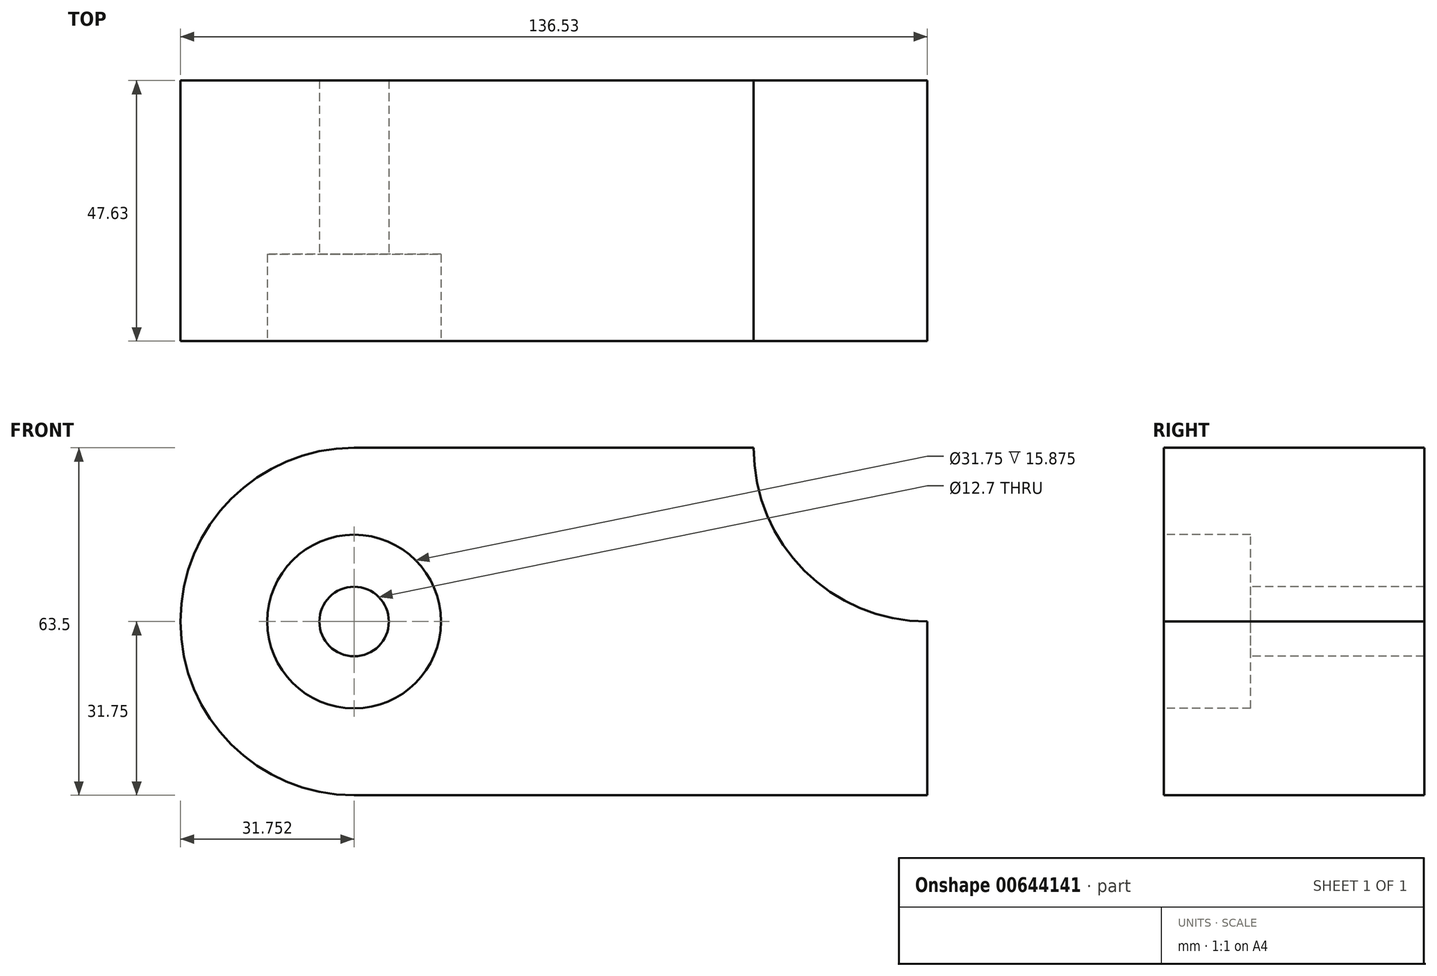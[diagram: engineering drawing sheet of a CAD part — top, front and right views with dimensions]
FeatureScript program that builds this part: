
annotation { "Feature Type Name" : "Feature", "Feature Type Description" : "" }
export const myFeature = defineFeature(function(context is Context, id is Id, definition is map)
    precondition{}
    {
        {
            var Q0;
            Q0=qCreatedBy(makeId("Front.planeOp"),FACE);
            var sketch = newSketch(context, id + "F0", { "sketchPlane" : qUnion([Q0])});
            skLineSegment(sketch, "E0.bottom", {"start": v(-52.39, -31.75) * mm, "end": v(52.39, -31.75) * mm});
            skPoint(sketch, "E0.middle", {"position": v(0, 0) * mm});
            skArc(sketch, "E1", {"start": v(-52.39, -31.75) * mm, "mid": v(-84.14, 0) * mm, "end": v(-52.39, 31.75) * mm});
            skArc(sketch, "E2", {"start": v(52.39, 0) * mm, "mid": v(29.94, 9.3) * mm, "end": v(20.64, 31.75) * mm});
            skLineSegment(sketch, "E3", {"start": v(20.64, 31.75) * mm, "end": v(-52.39, 31.75) * mm});
            skLineSegment(sketch, "E4", {"start": v(52.39, 0) * mm, "end": v(52.39, -31.75) * mm});
            skSolve(sketch);
        }
        {
            var Q0;
            Q0=makeQuery(id+"F0.imprint","IMPRINT",FACE,{"disambiguationData":[TD([[makeQuery(id+"F0.imprint","IMPRINT",EDGE,{"derivedFrom":sQuery(id+"F0.wireOp",EDGE,"E0.bottom")}),1.0]])]});
            extrude(context, id + "F1", {"entities" : qUnion([Q0]), "depth" : 47.62 * mm, "offsetDistance" : 25.4 * mm});
        }
        {
            var Q0;
            Q0=makeQuery(id+"F1.opExtrude","CAP_FACE",FACE,{"disambiguationData":[OSD([sQuery(id+"F0.wireOp",EDGE,"E0.bottom"),sQuery(id+"F0.wireOp",EDGE,"E1"),sQuery(id+"F0.wireOp",EDGE,"E2"),sQuery(id+"F0.wireOp",EDGE,"E3"),sQuery(id+"F0.wireOp",EDGE,"E4")])],"isStart":false});
            var sketch = newSketch(context, id + "F2", { "sketchPlane" : qUnion([Q0])});
            skPoint(sketch, "E5", {"position": v(-52.39, 0) * mm});
            skCircle(sketch, "E6", {"center": v(-52.39, 0) * mm, "radius": 15.88 * mm});
            skSolve(sketch);
        }
        {
            var Q0;
            Q0=makeQuery(id+"F2.imprint","IMPRINT",FACE,{"disambiguationData":[TD([[makeQuery(id+"F2.imprint","IMPRINT",EDGE,{"derivedFrom":sQuery(id+"F2.wireOp",EDGE,"E6")}),1.0]])]});
            extrude(context, id + "F3", {"entities" : qUnion([Q0]), "operationType" : NewBodyOperationType.REMOVE, "oppositeDirection" : true, "depth" : 15.88 * mm, "offsetDistance" : 25.4 * mm});
        }
        {
            var Q0;
            Q0=makeQuery(id+"F3.boolean.opBoolean","COPY",FACE,{"derivedFrom":makeQuery(id+"F3.opExtrude","CAP_FACE",FACE,{"disambiguationData":[OSD([sQuery(id+"F2.wireOp",EDGE,"E6")])],"isStart":false})});
            var sketch = newSketch(context, id + "F4", { "sketchPlane" : qUnion([Q0])});
            skPoint(sketch, "E7", {"position": v(-52.39, 0) * mm});
            skCircle(sketch, "E8", {"center": v(-52.39, 0) * mm, "radius": 6.35 * mm});
            skSolve(sketch);
        }
        {
            var Q0;
            Q0=makeQuery(id+"F4.imprint","IMPRINT",FACE,{"disambiguationData":[TD([[makeQuery(id+"F4.imprint","IMPRINT",EDGE,{"derivedFrom":sQuery(id+"F4.wireOp",EDGE,"E8")}),1.0]])]});
            extrude(context, id + "F5", {"entities" : qUnion([Q0]), "operationType" : NewBodyOperationType.REMOVE, "oppositeDirection" : true, "depth" : 34.3 * mm, "offsetDistance" : 25.4 * mm});
        }
    });
